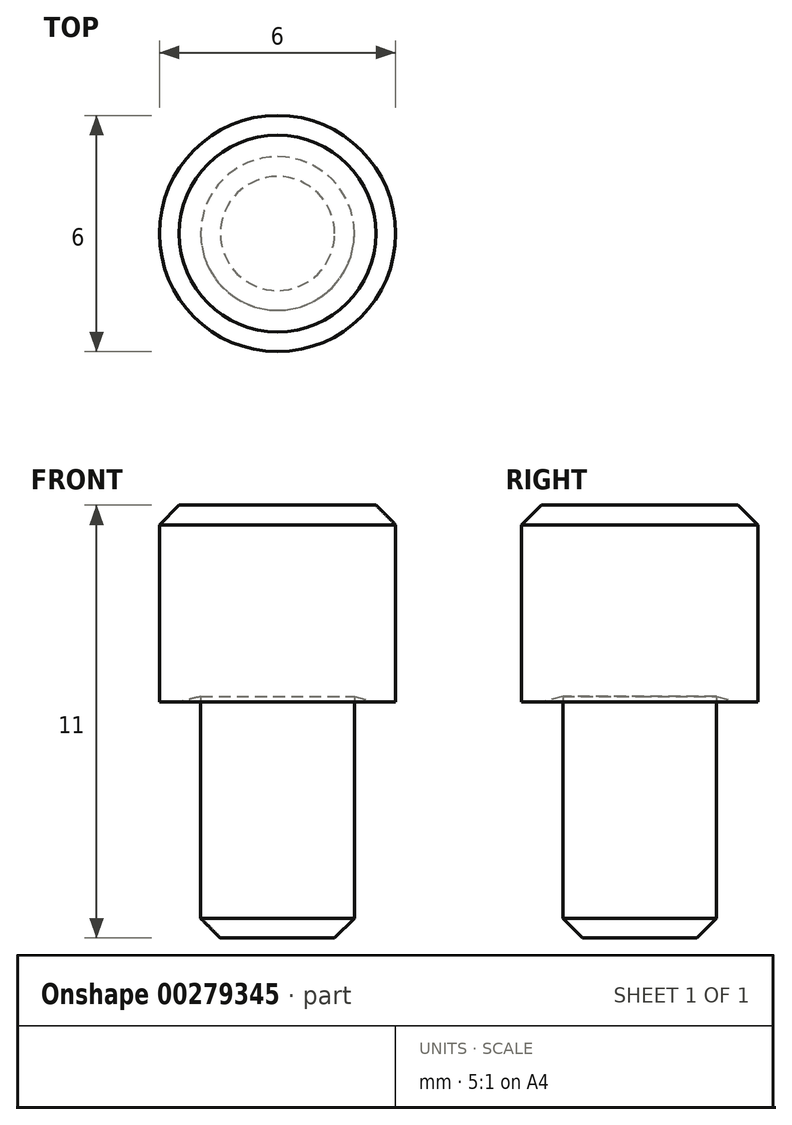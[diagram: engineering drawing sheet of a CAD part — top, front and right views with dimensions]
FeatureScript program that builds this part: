
annotation { "Feature Type Name" : "Feature", "Feature Type Description" : "" }
export const myFeature = defineFeature(function(context is Context, id is Id, definition is map)
    precondition{}
    {
        {
            var Q0;
            Q0=qCreatedBy(makeId("Front.planeOp"),FACE);
            var sketch = newSketch(context, id + "F0", { "sketchPlane" : qUnion([Q0])});
            skLineSegment(sketch, "E0.bottom", {"start": v(1.95, 0) * mm, "end": v(0, 0) * mm});
            skLineSegment(sketch, "E0.left", {"start": v(1.95, 0) * mm, "end": v(1.95, 6) * mm});
            skLineSegment(sketch, "E1.bottom", {"start": v(0, 11) * mm, "end": v(3, 11) * mm});
            skLineSegment(sketch, "E1.right", {"start": v(3, 11) * mm, "end": v(3, 6) * mm});
            skPoint(sketch, "E2", {"position": v(0, 11) * mm});
            skPoint(sketch, "E3", {"position": v(0, 0) * mm});
            skLineSegment(sketch, "E4.trimOffspring", {"start": v(1.95, 6) * mm, "end": v(3, 6) * mm});
            skLineSegment(sketch, "E5", {"start": v(0, 18.37) * mm, "end": v(0, -7.66) * mm});
            skSolve(sketch);
        }
        {
            var Q0;
            {var subQ1=sQuery(id+"F0.wireOp",EDGE,"E0.bottom");Q0=makeQuery(id+"F0.imprint","IMPRINT",FACE,{"disambiguationData":[TD([[makeQuery(id+"F0.imprint","IMPRINT",EDGE,{"derivedFrom":subQ1}),-1.0]])]});}
            var Q1;
            Q1=sQuery(id+"F0.wireOp",EDGE,"E5");
            revolve(context, id + "F1", {"entities" : qUnion([Q0]), "axis" : qUnion([Q1]), "revolveType" : RevolveType.FULL});
        }
        {
            var Q0;
            Q0=makeQuery(id+"F1.opRevolve","SWEPT_EDGE",EDGE,{"disambiguationData":[OSD([sQuery(id+"F0.wireOp",EDGE,"E1.bottom"),sQuery(id+"F0.wireOp",EDGE,"E1.right")])]});
            var Q1;
            Q1=makeQuery(id+"F1.opRevolve","SWEPT_FACE",FACE,{"disambiguationData":[OSD([sQuery(id+"F0.wireOp",EDGE,"E0.bottom")])]});
            chamfer(context, id + "F2", {"entities" : qUnion([Q0, Q1]), "width" : 0.5 * mm, "tangentPropagation" : true});
        }
        {
            var Q0;
            Q0=qCreatedBy(makeId("Front.planeOp"),FACE);
            var sketch = newSketch(context, id + "F3", { "sketchPlane" : qUnion([Q0])});
            skPoint(sketch, "E6", {"position": v(1.95, 6) * mm});
            skLineSegment(sketch, "E7", {"start": v(2.5, 6) * mm, "end": v(1.95, 6) * mm});
            skLineSegment(sketch, "E8", {"start": v(2.5, 6) * mm, "end": v(1.95, 6.14) * mm});
            skLineSegment(sketch, "E9", {"start": v(1.95, 6) * mm, "end": v(1.95, 6.14) * mm});
            skLineSegment(sketch, "E10", {"start": v(0, 12.66) * mm, "end": v(0, -1.84) * mm});
            skSolve(sketch);
        }
        {
            var Q0;
            Q0 = qSketchRegion(id + "F3", true);
            var Q1;
            Q1=sQuery(id+"F3.wireOp",EDGE,"E10");
            revolve(context, id + "F4", {"operationType" : NewBodyOperationType.REMOVE, "entities" : qUnion([Q0]), "axis" : qUnion([Q1]), "revolveType" : RevolveType.FULL, "oppositeDirection" : true});
        }
    });
